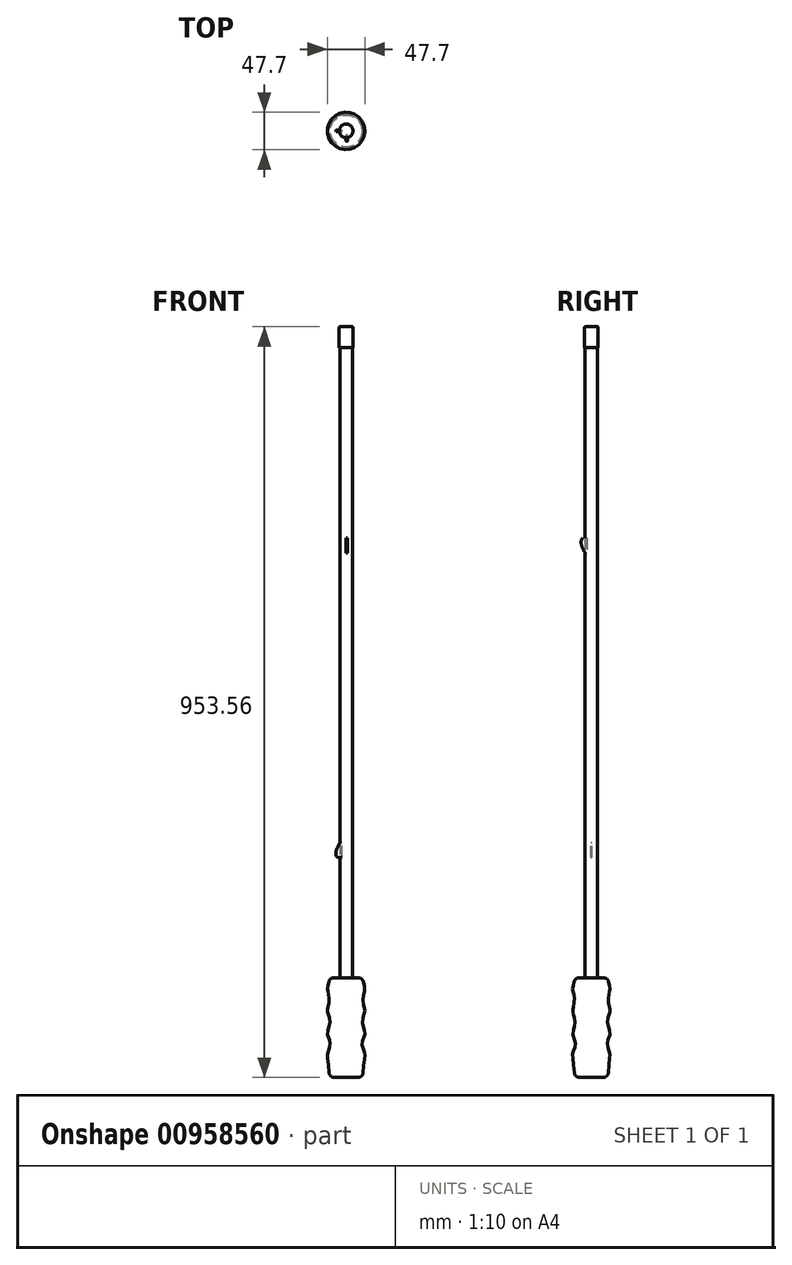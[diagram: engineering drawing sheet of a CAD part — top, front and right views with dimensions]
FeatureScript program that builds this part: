
annotation { "Feature Type Name" : "Feature", "Feature Type Description" : "" }
export const myFeature = defineFeature(function(context is Context, id is Id, definition is map)
    precondition{}
    {
        {
            var Q0;
            Q0=qCreatedBy(makeId("Front.planeOp"),FACE);
            var sketch = newSketch(context, id + "F0", { "sketchPlane" : qUnion([Q0])});
            skLineSegment(sketch, "E0", {"start": v(0, 66.17) * mm, "end": v(0, -60.62) * mm});
            skLineSegment(sketch, "E1", {"start": v(0, -60.62) * mm, "end": v(15.24, -60.62) * mm});
            skFitSpline(sketch, "E2", {"points": [v(21.32, -60.62) * mm, v(23.46, -34.97) * mm, v(23.46, -28.86) * mm, v(20.4, -18.17) * mm, v(23.46, -6.87) * mm, v(23.46, -1.98) * mm, v(20.7, 10.23) * mm, v(23.46, 22.45) * mm, v(23.46, 26.11) * mm, v(21.63, 38.94) * mm, v(23.46, 49.93) * mm, v(23.46, 53.6) * mm, v(21.32, 65.8) * mm], "startDerivative": vector(0, 126.12) * mm, "endDerivative": vector(0, 126.12) * mm});
            skLineSegment(sketch, "E3", {"start": v(15.77, 65.9) * mm, "end": v(0, 66.17) * mm});
            skArc(sketch, "E4.filletArc", {"start": v(15.24, -60.62) * mm, "mid": v(19.58, -58.9) * mm, "end": v(21.58, -54.7) * mm});
            skArc(sketch, "E5.filletArc", {"start": v(21.9, 60.73) * mm, "mid": v(19.75, 64.4) * mm, "end": v(15.77, 65.9) * mm});
            skPoint(sketch, "E6", {"position": v(0, 0) * mm});
            skPoint(sketch, "E6.positionSnap0", {"position": v(0, 2.78) * mm});
            skSolve(sketch);
        }
        {
            var Q0;
            Q0=makeQuery(id+"F0.imprint","IMPRINT",FACE,{"disambiguationData":[TD([[makeQuery(id+"F0.imprint","IMPRINT",EDGE,{"derivedFrom":sQuery(id+"F0.wireOp",EDGE,"E0")}),1.0]])]});
            var Q1;
            Q1=sQuery(id+"F0.wireOp",EDGE,"E0");
            revolve(context, id + "F1", {"surfaceOperationType" : NewSurfaceOperationType.NEW, "entities" : qUnion([Q0]), "axis" : qUnion([Q1]), "revolveType" : RevolveType.FULL});
        }
        {
            var Q0;
            Q0=qCreatedBy(makeId("Top.planeOp"),FACE);
            var sketch = newSketch(context, id + "F2", { "sketchPlane" : qUnion([Q0])});
            skCircle(sketch, "E7", {"center": v(0, 0) * mm, "radius": 7.94 * mm});
            skSolve(sketch);
        }
        {
            var Q0;
            Q0 = qSketchRegion(id + "F2", true);
            extrude(context, id + "F3", {"entities" : qUnion([Q0]), "operationType" : NewBodyOperationType.ADD, "depth" : 892.17 * mm, "offsetDistance" : 25.4 * mm});
        }
        {
            var Q0;
            Q0=qCreatedBy(makeId("Front.planeOp"),FACE);
            var sketch = newSketch(context, id + "F4", { "sketchPlane" : qUnion([Q0])});
            skLineSegment(sketch, "E8", {"start": v(0, 63.5) * mm, "end": v(0, 218.57) * mm});
            skLineSegment(sketch, "E9", {"start": v(0, 218.57) * mm, "end": v(-7.94, 218.57) * mm});
            skLineSegment(sketch, "E10", {"start": v(-7.94, 218.57) * mm, "end": v(-11.11, 218.57) * mm});
            skFitSpline(sketch, "E11", {"points": [v(-11.11, 218.57) * mm, v(-7.94, 237.62) * mm], "startDerivative": vector(-14.81, 18.97) * mm, "endDerivative": vector(6.85, 13.55) * mm});
            skLineSegment(sketch, "E12.bottom", {"start": v(-7.94, 218.57) * mm, "end": v(-5.4, 218.57) * mm});
            skLineSegment(sketch, "E12.top", {"start": v(-7.94, 237.62) * mm, "end": v(-5.4, 237.62) * mm});
            skLineSegment(sketch, "E12.right", {"start": v(-5.4, 218.57) * mm, "end": v(-5.4, 237.62) * mm});
            skSolve(sketch);
        }
        {
            var Q0;
            {var subQ0=sQuery(id+"F4.wireOp",EDGE,"E10");Q0=makeQuery(id+"F4.imprint","IMPRINT",FACE,{"disambiguationData":[TD([[makeQuery(id+"F4.imprint","IMPRINT",EDGE,{"derivedFrom":subQ0}),-1.0]])]});}
            extrude(context, id + "F5", {"entities" : qUnion([Q0]), "depth" : 1.59 * mm, "offsetDistance" : 25.4 * mm, "symmetric" : true});
        }
        {
            var Q0;
            Q0=qCreatedBy(makeId("Right.planeOp"),FACE);
            var sketch = newSketch(context, id + "F6", { "sketchPlane" : qUnion([Q0])});
            skLineSegment(sketch, "E13.top", {"start": v(-2.86, 605.8) * mm, "end": v(-5.4, 605.8) * mm});
            skLineSegment(sketch, "E13.right", {"start": v(-5.4, 624.84) * mm, "end": v(-5.4, 605.8) * mm});
            skLineSegment(sketch, "E14.MirrorCS", {"start": v(-7.94, 605.8) * mm, "end": v(-5.4, 605.8) * mm});
            skLineSegment(sketch, "E15.MirrorCS", {"start": v(-7.94, 605.8) * mm, "end": v(-5.4, 605.8) * mm, "construction": true});
            skLineSegment(sketch, "E16.MirrorCS", {"start": v(-7.94, 624.84) * mm, "end": v(-5.4, 624.84) * mm});
            skFitSpline(sketch, "E17.MirrorCS", {"points": [v(-11.11, 624.84) * mm, v(-7.94, 605.8) * mm], "startDerivative": vector(-14.81, -18.97) * mm, "endDerivative": vector(6.85, -13.55) * mm});
            skLineSegment(sketch, "E18.MirrorCS", {"start": v(-7.94, 624.84) * mm, "end": v(-11.11, 624.84) * mm});
            skLineSegment(sketch, "E19.MirrorCS", {"start": v(-7.94, 624.84) * mm, "end": v(-7.94, 605.8) * mm, "construction": true});
            skLineSegment(sketch, "E20", {"start": v(0, 0) * mm, "end": v(0, 69.58) * mm});
            skLineSegment(sketch, "E21", {"start": v(0, 0) * mm, "end": v(0, 66.04) * mm});
            skLineSegment(sketch, "E22", {"start": v(0, 66.04) * mm, "end": v(0, 624.84) * mm});
            skLineSegment(sketch, "E23", {"start": v(0, 624.84) * mm, "end": v(-7.94, 624.84) * mm});
            skSolve(sketch);
        }
        {
            var Q0;
            Q0=makeQuery(id+"F6.imprint","IMPRINT",FACE,{"disambiguationData":[TD([[makeQuery(id+"F6.imprint","IMPRINT",EDGE,{"derivedFrom":sQuery(id+"F6.wireOp",EDGE,"E13.right")}),-1.0]])]});
            extrude(context, id + "F7", {"entities" : qUnion([Q0]), "depth" : 1.59 * mm, "offsetDistance" : 25.4 * mm});
        }
        {
            var Q0;
            Q0=makeQuery(id+"F3.opExtrude","CAP_FACE",FACE,{"disambiguationData":[OSD([sQuery(id+"F2.wireOp",EDGE,"E7")])],"isStart":false});
            var sketch = newSketch(context, id + "F8", { "sketchPlane" : qUnion([Q0])});
            skCircle(sketch, "E24", {"center": v(0, 0) * mm, "radius": 8.7 * mm});
            skCircle(sketch, "E25", {"center": v(0, 0) * mm, "radius": 7.94 * mm});
            skSolve(sketch);
        }
        {
            var Q0;
            Q0=makeQuery(id+"F8.imprint","IMPRINT",FACE,{"disambiguationData":[TD([[makeQuery(id+"F8.imprint","IMPRINT",EDGE,{"derivedFrom":sQuery(id+"F8.wireOp",EDGE,"E24")}),1.0]])]});
            var Q1;
            Q1=makeQuery(id+"F8.imprint","IMPRINT",FACE,{"disambiguationData":[TD([[makeQuery(id+"F8.imprint","IMPRINT",EDGE,{"derivedFrom":sQuery(id+"F8.wireOp",EDGE,"E25")}),1.0]])]});
            extrude(context, id + "F9", {"entities" : qUnion([Q0, Q1]), "depth" : 0.77 * mm, "offsetDistance" : 25.4 * mm});
        }
        {
            var Q0;
            Q0=makeQuery(id+"F8.imprint","IMPRINT",FACE,{"disambiguationData":[TD([[makeQuery(id+"F8.imprint","IMPRINT",EDGE,{"derivedFrom":sQuery(id+"F8.wireOp",EDGE,"E24")}),1.0]])]});
            extrude(context, id + "F10", {"entities" : qUnion([Q0]), "operationType" : NewBodyOperationType.ADD, "oppositeDirection" : true, "depth" : 25.4 * mm, "offsetDistance" : 25.4 * mm});
        }
        {
            var Q0;
            Q0=makeQuery(id+"F9.opExtrude","CAP_EDGE",EDGE,{"disambiguationData":[OSD([sQuery(id+"F8.wireOp",EDGE,"E24")])],"isStart":false});
            fillet(context, id + "F11", {"entities" : qUnion([Q0]), "radius" : 0.77 * mm, "tangentPropagation" : true, "allowEdgeOverflow" : false});
        }
    });
